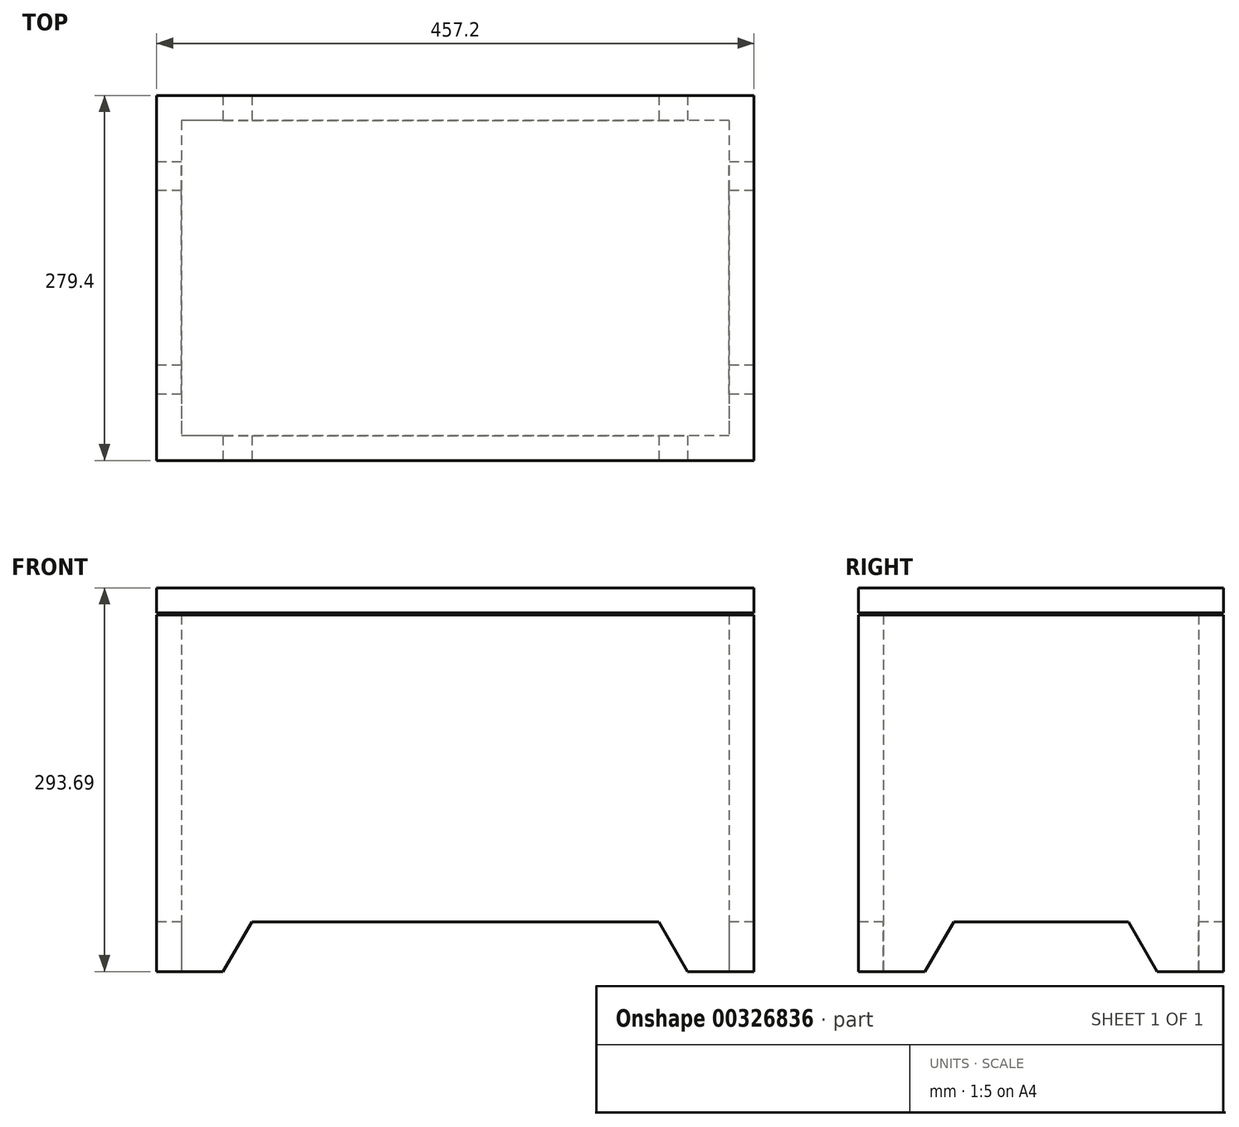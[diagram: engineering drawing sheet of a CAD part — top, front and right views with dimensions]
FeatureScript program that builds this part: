
annotation { "Feature Type Name" : "Feature", "Feature Type Description" : "" }
export const myFeature = defineFeature(function(context is Context, id is Id, definition is map)
    precondition{}
    {
        {
            var Q0;
            Q0=qCreatedBy(makeId("Top.planeOp"),FACE);
            var sketch = newSketch(context, id + "F0", { "sketchPlane" : qUnion([Q0])});
            skLineSegment(sketch, "E0.bottom", {"start": v(228.6, 139.7) * mm, "end": v(-228.6, 139.7) * mm});
            skLineSegment(sketch, "E0.top", {"start": v(228.6, -139.7) * mm, "end": v(-228.6, -139.7) * mm});
            skLineSegment(sketch, "E0.left", {"start": v(228.6, 139.7) * mm, "end": v(228.6, -139.7) * mm});
            skLineSegment(sketch, "E0.right", {"start": v(-228.6, 139.7) * mm, "end": v(-228.6, -139.7) * mm});
            skPoint(sketch, "E0.middle", {"position": v(0, 0) * mm});
            skSolve(sketch);
        }
        {
            var Q0;
            Q0=makeQuery(id+"F0.imprint","IMPRINT",FACE,{"disambiguationData":[TD([[makeQuery(id+"F0.imprint","IMPRINT",EDGE,{"derivedFrom":sQuery(id+"F0.wireOp",EDGE,"E0.bottom")}),1.0]])]});
            extrude(context, id + "F1", {"entities" : qUnion([Q0]), "depth" : 273.05 * mm});
        }
        {
            var Q0;
            Q0=makeQuery(id+"F1.opExtrude","CAP_FACE",FACE,{"disambiguationData":[OSD([sQuery(id+"F0.wireOp",EDGE,"E0.bottom"),sQuery(id+"F0.wireOp",EDGE,"E0.top"),sQuery(id+"F0.wireOp",EDGE,"E0.left"),sQuery(id+"F0.wireOp",EDGE,"E0.right")])],"isStart":false});
            var Q1;
            Q1=makeQuery(id+"F1.opExtrude","CAP_FACE",FACE,{"disambiguationData":[OSD([sQuery(id+"F0.wireOp",EDGE,"E0.bottom"),sQuery(id+"F0.wireOp",EDGE,"E0.top"),sQuery(id+"F0.wireOp",EDGE,"E0.left"),sQuery(id+"F0.wireOp",EDGE,"E0.right")])],"isStart":true});
            shell(context, id + "F2", {"entities" : qUnion([Q0, Q1]), "thickness" : 19.05 * mm});
        }
        {
            var Q0;
            Q0=makeQuery(id+"F1.opExtrude","SWEPT_FACE",FACE,{"disambiguationData":[OSD([sQuery(id+"F0.wireOp",EDGE,"E0.top")])]});
            var sketch = newSketch(context, id + "F3", { "sketchPlane" : qUnion([Q0])});
            skLineSegment(sketch, "E1", {"start": v(-177.8, 0) * mm, "end": v(-155.8, 38.1) * mm});
            skLineSegment(sketch, "E2", {"start": v(-155.8, 38.1) * mm, "end": v(155.8, 38.1) * mm});
            skLineSegment(sketch, "E3", {"start": v(155.8, 38.1) * mm, "end": v(177.8, 0) * mm});
            skLineSegment(sketch, "E4", {"start": v(177.8, 0) * mm, "end": v(-177.8, 0) * mm});
            skSolve(sketch);
        }
        {
            var Q0;
            Q0 = qSketchRegion(id + "F3", true);
            extrude(context, id + "F4", {"entities" : qUnion([Q0]), "operationType" : NewBodyOperationType.REMOVE, "endBound" : BoundingType.THROUGH_ALL, "oppositeDirection" : true, "depth" : 25.4 * mm});
        }
        {
            var Q0;
            Q0=makeQuery(id+"F1.opExtrude","SWEPT_FACE",FACE,{"disambiguationData":[OSD([sQuery(id+"F0.wireOp",EDGE,"E0.right")])]});
            var sketch = newSketch(context, id + "F5", { "sketchPlane" : qUnion([Q0])});
            skLineSegment(sketch, "E5", {"start": v(88.9, 0) * mm, "end": v(-88.9, 0) * mm});
            skLineSegment(sketch, "E6", {"start": v(-88.9, 0) * mm, "end": v(-66.9, 38.1) * mm});
            skLineSegment(sketch, "E7", {"start": v(-66.9, 38.1) * mm, "end": v(66.9, 38.1) * mm});
            skLineSegment(sketch, "E8", {"start": v(66.9, 38.1) * mm, "end": v(88.9, 0) * mm});
            skSolve(sketch);
        }
        {
            var Q0;
            Q0 = qSketchRegion(id + "F5", true);
            extrude(context, id + "F6", {"entities" : qUnion([Q0]), "operationType" : NewBodyOperationType.REMOVE, "endBound" : BoundingType.THROUGH_ALL, "oppositeDirection" : true, "depth" : 25.4 * mm});
        }
        {
            var Q0;
            Q0=qCreatedBy(makeId("Front.planeOp"),FACE);
            var sketch = newSketch(context, id + "F7", { "sketchPlane" : qUnion([Q0])});
            skLineSegment(sketch, "E9.bottom", {"start": v(-228.6, 293.69) * mm, "end": v(228.6, 293.69) * mm});
            skLineSegment(sketch, "E9.top", {"start": v(-228.6, 274.64) * mm, "end": v(228.6, 274.64) * mm});
            skLineSegment(sketch, "E9.left", {"start": v(-228.6, 293.69) * mm, "end": v(-228.6, 274.64) * mm});
            skLineSegment(sketch, "E9.right", {"start": v(228.6, 293.69) * mm, "end": v(228.6, 274.64) * mm});
            skSolve(sketch);
        }
        {
            var Q0;
            Q0 = qSketchRegion(id + "F7", true);
            extrude(context, id + "F8", {"entities" : qUnion([Q0]), "endBound" : BoundingType.SYMMETRIC, "depth" : 279.4 * mm});
        }
    });
